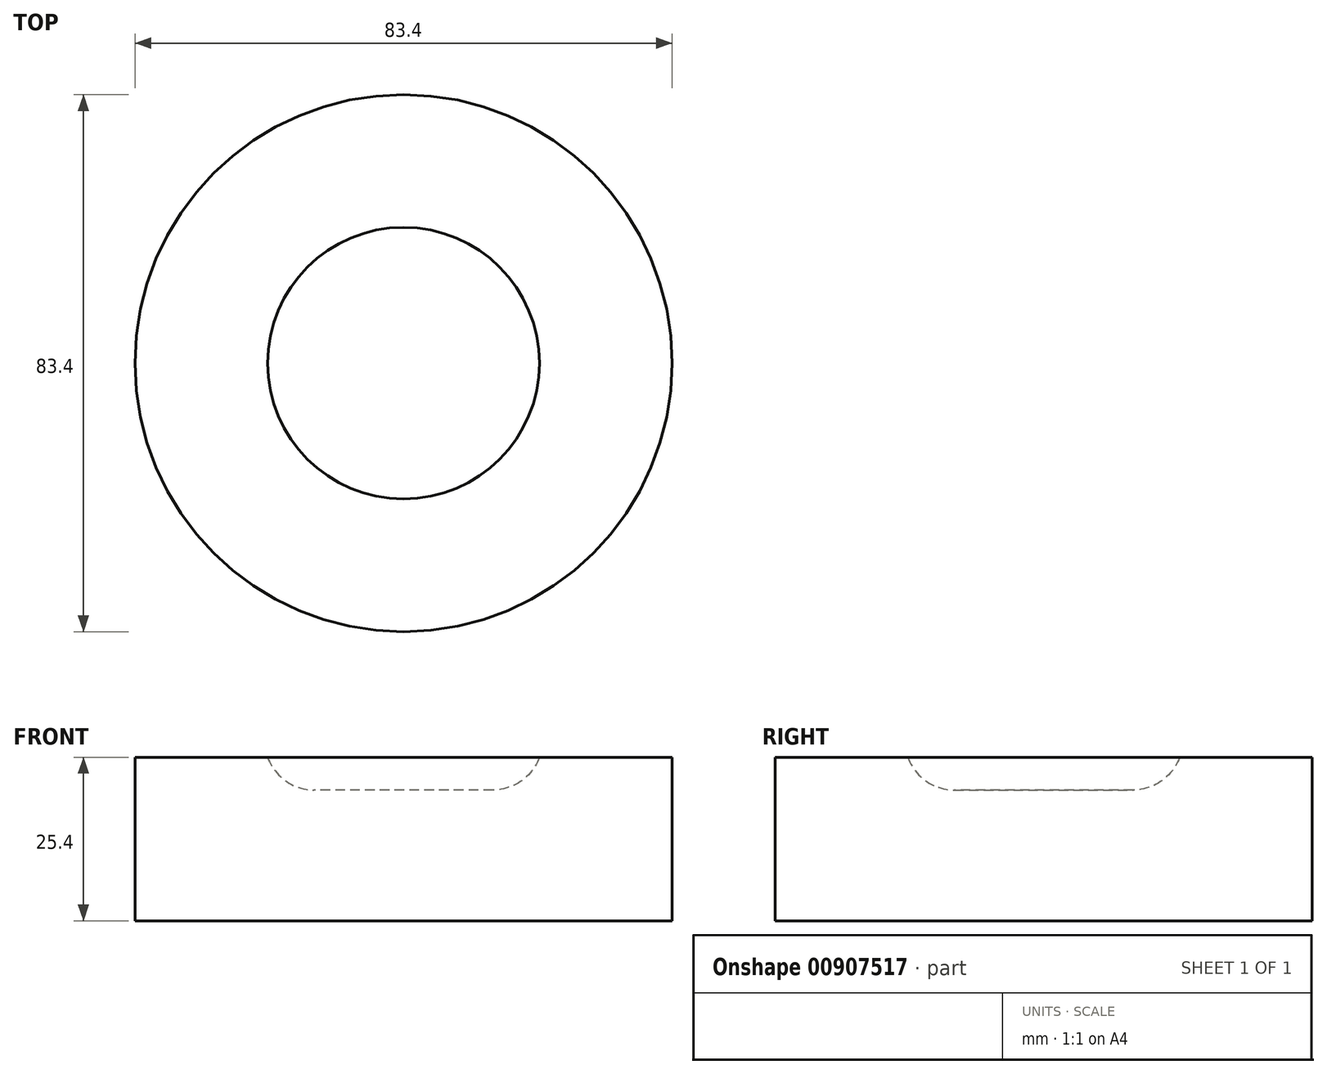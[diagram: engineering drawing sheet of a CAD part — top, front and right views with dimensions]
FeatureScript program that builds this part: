
annotation { "Feature Type Name" : "Feature", "Feature Type Description" : "" }
export const myFeature = defineFeature(function(context is Context, id is Id, definition is map)
    precondition{}
    {
        {
            var Q0;
            Q0=qCreatedBy(makeId("Top.planeOp"),FACE);
            var sketch = newSketch(context, id + "F0", { "sketchPlane" : qUnion([Q0])});
            skCircle(sketch, "E0", {"center": v(0, 0) * mm, "radius": 41.7 * mm});
            skSolve(sketch);
        }
        {
            var Q0;
            Q0 = qSketchRegion(id + "F0", true);
            extrude(context, id + "F1", {"entities" : qUnion([Q0]), "oppositeDirection" : true, "depth" : 25.4 * mm, "offsetDistance" : 25.4 * mm});
        }
        {
            var Q0;
            Q0=makeQuery(id+"F1.opExtrude","CAP_FACE",FACE,{"disambiguationData":[OSD([sQuery(id+"F0.wireOp",EDGE,"E0")])],"isStart":true});
            var sketch = newSketch(context, id + "F2", { "sketchPlane" : qUnion([Q0])});
            skCircle(sketch, "E1", {"center": v(0, 0) * mm, "radius": 21.1 * mm});
            skSolve(sketch);
        }
        {
            var Q0;
            Q0 = qSketchRegion(id + "F2", true);
            var Q1;
            Q1=sQuery(id+"F2.wireOp",EDGE,"E1");
            extrude(context, id + "F3", {"entities" : qUnion([Q0]), "operationType" : NewBodyOperationType.REMOVE, "surfaceEntities" : qUnion([Q1]), "oppositeDirection" : true, "depth" : 5.08 * mm, "offsetDistance" : 25.4 * mm});
        }
        {
            var Q0;
            Q0=makeQuery(id+"F3.boolean.opBoolean","COPY",EDGE,{"derivedFrom":makeQuery(id+"F3.opExtrude","CAP_EDGE",EDGE,{"disambiguationData":[OSD([sQuery(id+"F2.wireOp",EDGE,"E1")])],"isStart":false})});
            fillet(context, id + "F4", {"entities" : qUnion([Q0]), "radius" : 7.62 * mm, "tangentPropagation" : true, "allowEdgeOverflow" : false});
        }
    });
